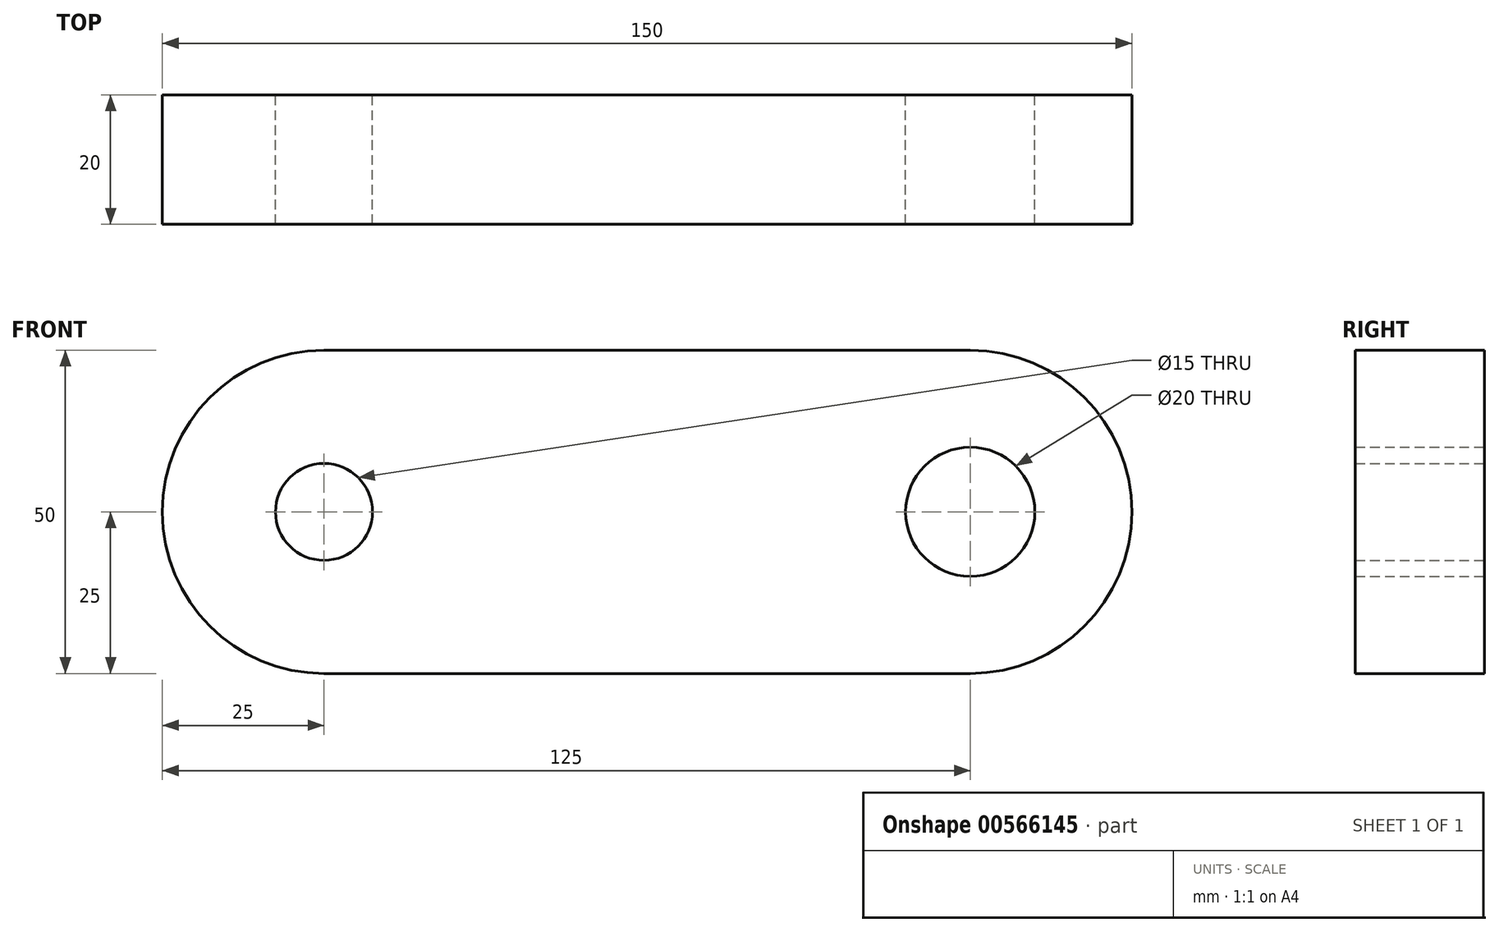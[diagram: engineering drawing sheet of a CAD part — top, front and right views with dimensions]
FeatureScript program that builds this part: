
annotation { "Feature Type Name" : "Feature", "Feature Type Description" : "" }
export const myFeature = defineFeature(function(context is Context, id is Id, definition is map)
    precondition{}
    {
        {
            var Q0;
            Q0=qCreatedBy(makeId("Front.planeOp"),FACE);
            var sketch = newSketch(context, id + "F0", { "sketchPlane" : qUnion([Q0])});
            skArc(sketch, "E0", {"start": v(0, 25) * mm, "mid": v(-25, 0) * mm, "end": v(0, -25) * mm});
            skArc(sketch, "E1", {"start": v(100, -25) * mm, "mid": v(125, 0) * mm, "end": v(100, 25) * mm});
            skLineSegment(sketch, "E2", {"start": v(0, 25) * mm, "end": v(100, 25) * mm});
            skLineSegment(sketch, "E3", {"start": v(100, -25) * mm, "end": v(0, -25) * mm});
            skCircle(sketch, "E4", {"center": v(0, 0) * mm, "radius": 7.5 * mm});
            skCircle(sketch, "E5", {"center": v(100, 0) * mm, "radius": 10 * mm});
            skSolve(sketch);
        }
        {
            var Q0;
            Q0 = qSketchRegion(id + "F0", true);
            extrude(context, id + "F1", {"entities" : qUnion([Q0]), "endBound" : BoundingType.SYMMETRIC, "depth" : 20 * mm, "offsetDistance" : 25.4 * mm});
        }
    });
